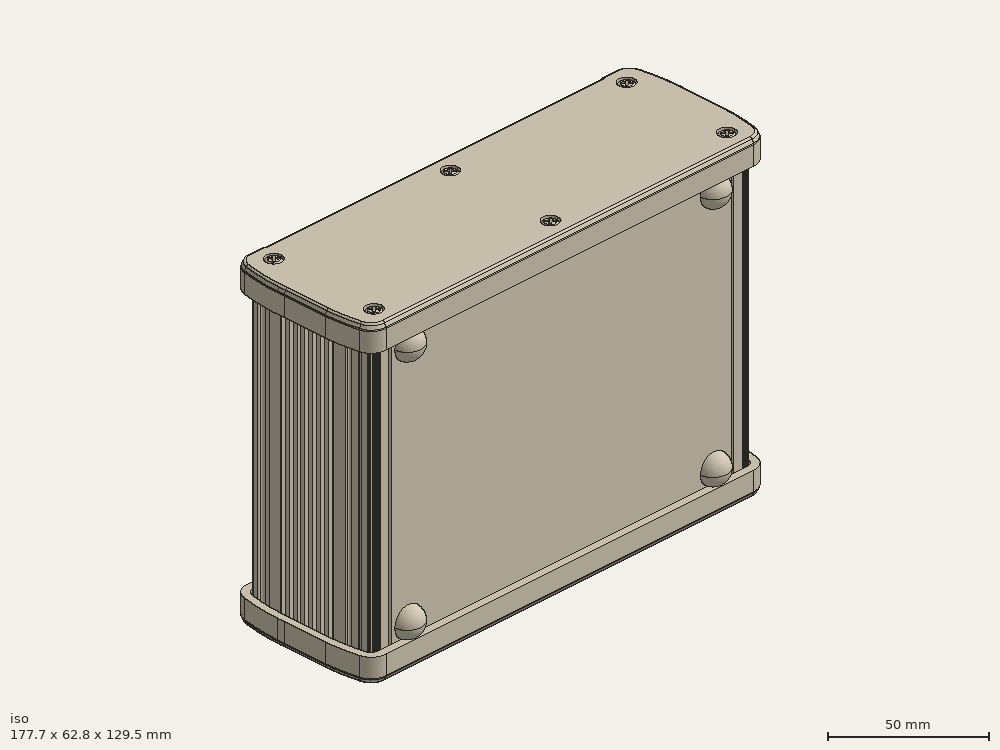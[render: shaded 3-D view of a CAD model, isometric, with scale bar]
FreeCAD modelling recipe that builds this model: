
FCSTD DOCUMENT  (FreeCAD 0.19R24276 (Git))
Label: loraPy
License: All rights reserved
LicenseURL: http://en.wikipedia.org/wiki/All_rights_reserved
objects: Part::Cylinder×12, Part::Box×9, Part::MultiFuse×6, Part::Cut×3, Part::Feature×2
note: 32 computed .brp shape members not serialized (recipe doc carries the construction recipe); baked Part::Feature solids carry a one-line shape summary decoded from their .brp

FEATURE [Part::Box] Box  label="base"
  AttacherType = Attacher::AttachEngine3D
  Height = 100
  Length = 160
  Placement = pos=(0,14.6,4) rot=(0,0,1;0rad)
  Width = 1.6
FEATURE [Part::Feature] Feature  label="EX-64-002"
  Placement = pos=(80,2.7,54) rot=(0,0,1;0rad)
  shape: bbox 178.8 x 63.35 x 129.6 mm, 1628 faces, 33 solids (baked)
FEATURE [Part::Box] Box001  label="base001"
  AttacherType = Attacher::AttachEngine3D
  Height = 100
  Length = 155
  Placement = pos=(2.5,11.7,4) rot=(0,0,1;0rad)
  Width = 2.9
FEATURE [Part::Feature] Feature001  label="Odroid-C1+002"
  Placement = pos=(48,2,72) rot=(-1,0,0;3.14159rad)
  shape: bbox 87.6 x 21.76 x 59.54 mm, 16908 faces, 571 solids (baked)
FEATURE [Part::Box] Box002  label="e5mini"
  AttacherType = Attacher::AttachEngine3D
  Height = 23
  Length = 61
  Width = 6
FEATURE [Part::Cylinder] Cylinder  label="m2s"
  Angle = 360
  AttacherType = Attacher::AttachEngine3D
  Height = 10
  Placement = pos=(14,0,3) rot=(1,0,0;1.5708rad)
  Radius = 1.2
FEATURE [Part::Cylinder] Cylinder001  label="m2s001"
  Angle = 360
  AttacherType = Attacher::AttachEngine3D
  Height = 10
  Placement = pos=(14,0,20) rot=(1,0,0;1.5708rad)
  Radius = 1.2
FEATURE [Part::Cylinder] Cylinder002  label="m2s002"
  Angle = 360
  AttacherType = Attacher::AttachEngine3D
  Height = 10
  Placement = pos=(49,0,20) rot=(1,0,0;1.5708rad)
  Radius = 1.2
FEATURE [Part::Cylinder] Cylinder003  label="m2s003"
  Angle = 360
  AttacherType = Attacher::AttachEngine3D
  Height = 10
  Placement = pos=(49,0,3) rot=(1,0,0;1.5708rad)
  Radius = 1.2
FEATURE [Part::MultiFuse] Fusion  label="e5MiniCuts"
  Placement = pos=(0,6,0) rot=(0,0,1;0rad)
  Shapes = -> [Cylinder,Cylinder001,Cylinder002,Cylinder003]
FEATURE [Part::Cut] Cut  label="e5Mini"
  Base = -> Box002
  Placement = pos=(30,5.7,15) rot=(0,0,1;0rad)
  Tool = -> Fusion
FEATURE [Part::MultiFuse] Fusion001  label="base002"
  Shapes = -> [Box001,Box]
FEATURE [Part::Cylinder] Cylinder004  label="m2s004"
  Angle = 360
  AttacherType = Attacher::AttachEngine3D
  Height = 10
  Placement = pos=(49,0,3) rot=(1,0,0;1.5708rad)
  Radius = 1.6
FEATURE [Part::Cylinder] Cylinder005  label="m2s005"
  Angle = 360
  AttacherType = Attacher::AttachEngine3D
  Height = 10
  Placement = pos=(14,0,20) rot=(1,0,0;1.5708rad)
  Radius = 1.6
FEATURE [Part::Cylinder] Cylinder006  label="m2s006"
  Angle = 360
  AttacherType = Attacher::AttachEngine3D
  Height = 10
  Placement = pos=(14,0,3) rot=(1,0,0;1.5708rad)
  Radius = 1.6
FEATURE [Part::Cylinder] Cylinder007  label="m2s007"
  Angle = 360
  AttacherType = Attacher::AttachEngine3D
  Height = 10
  Placement = pos=(49,0,20) rot=(1,0,0;1.5708rad)
  Radius = 1.6
FEATURE [Part::MultiFuse] Fusion002  label="e5MiniCuts001"
  Placement = pos=(30,16.2,15) rot=(0,0,1;0rad)
  Shapes = -> [Cylinder006,Cylinder005,Cylinder007,Cylinder004]
FEATURE [Part::Cylinder] Cylinder008  label="m2s008"
  Angle = 360
  AttacherType = Attacher::AttachEngine3D
  Height = 10
  Placement = pos=(9,9.9e-15,47.5) rot=(1,0,0;1.5708rad)
  Radius = 2
FEATURE [Part::Cylinder] Cylinder009  label="m2s009"
  Angle = 360
  AttacherType = Attacher::AttachEngine3D
  Height = 10
  Placement = pos=(67,9.9e-15,47.5) rot=(1,0,0;1.5708rad)
  Radius = 2
FEATURE [Part::Cylinder] Cylinder010  label="m2s010"
  Angle = 360
  AttacherType = Attacher::AttachEngine3D
  Height = 10
  Placement = pos=(67,2.08e-14,96.5) rot=(1,0,0;1.5708rad)
  Radius = 2
FEATURE [Part::Cylinder] Cylinder011  label="m2s011"
  Angle = 360
  AttacherType = Attacher::AttachEngine3D
  Height = 10
  Placement = pos=(9,2.08e-14,96.5) rot=(1,0,0;1.5708rad)
  Radius = 2
FEATURE [Part::MultiFuse] Fusion003  label="c1Cuts"
  Placement = pos=(0,16.4,0) rot=(0,0,1;0rad)
  Shapes = -> [Cylinder011,Cylinder008,Cylinder009,Cylinder010]
FEATURE [Part::MultiFuse] Fusion004  label="baseCuts"
  Shapes = -> [Fusion002,Fusion003]
FEATURE [Part::Cut] Cut001  label="base003"
  Base = -> Fusion001
  Tool = -> Fusion004
FEATURE [Part::Box] Box004  label="cuts001"
  AttacherType = Attacher::AttachEngine3D
  Height = 36
  Length = 110
  Placement = pos=(50,10,54) rot=(0,0,1;0rad)
  Width = 10
FEATURE [Part::Box] Box005  label="cuts002"
  AttacherType = Attacher::AttachEngine3D
  Height = 30
  Length = 70
  Placement = pos=(90,10,14.6) rot=(0,0,1;0rad)
  Width = 10
FEATURE [Part::Box] Box006  label="cuts003"
  AttacherType = Attacher::AttachEngine3D
  Height = 25
  Length = 35
  Placement = pos=(0,10,14.6) rot=(0,0,1;0rad)
  Width = 10
FEATURE [Part::Box] Box007  label="cuts004"
  AttacherType = Attacher::AttachEngine3D
  Height = 36
  Length = 35
  Placement = pos=(0,10,54.2) rot=(0,0,1;0rad)
  Width = 10
FEATURE [Part::Box] Box008  label="cuts005"
  AttacherType = Attacher::AttachEngine3D
  Height = 50
  Length = 85
  Placement = pos=(75,10,54) rot=(0,0,1;0rad)
  Width = 10
FEATURE [Part::Box] Box009  label="cuts006"
  AttacherType = Attacher::AttachEngine3D
  Height = 35
  Length = 22
  Placement = pos=(50,10,4) rot=(0,0,1;0rad)
  Width = 10
FEATURE [Part::MultiFuse] Fusion005  label="cuts"
  Shapes = -> [Box004,Box005,Box006,Box007,Box008,Box009]
FEATURE [Part::Cut] Cut002
  Base = -> Cut001
  Tool = -> Fusion005
